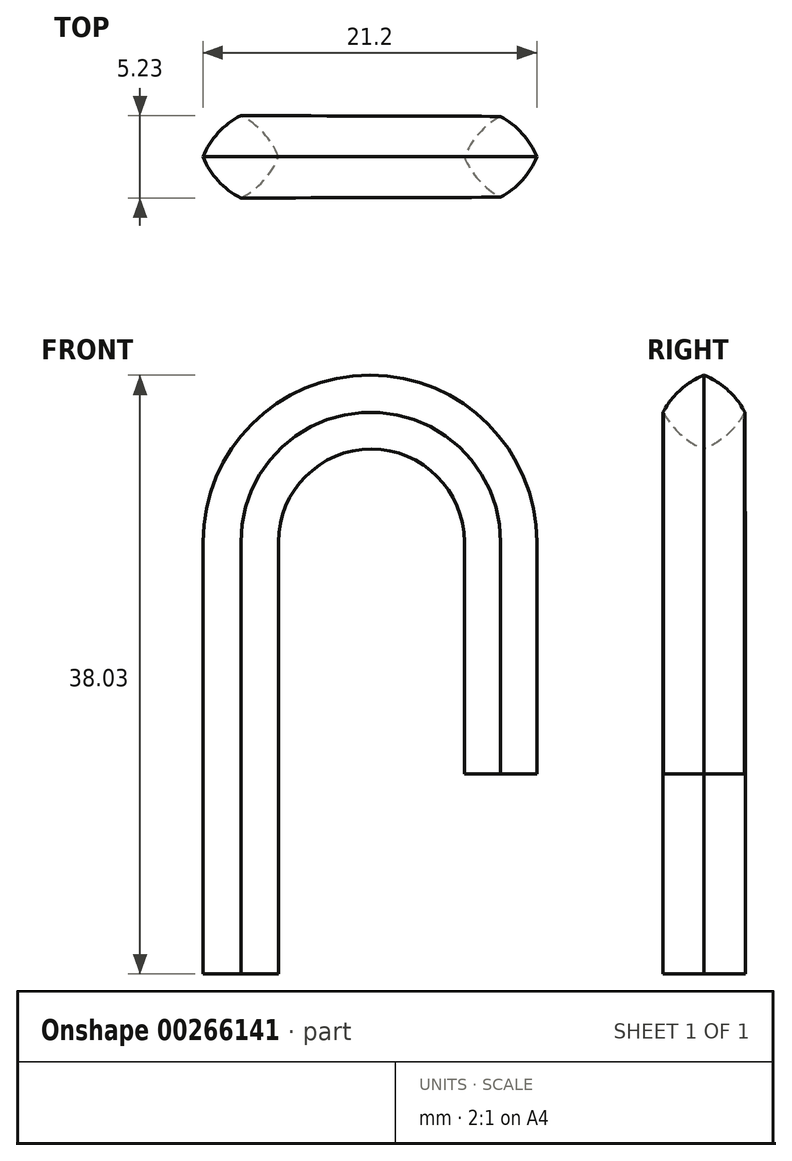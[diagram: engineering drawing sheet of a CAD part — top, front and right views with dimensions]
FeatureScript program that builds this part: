
annotation { "Feature Type Name" : "Feature", "Feature Type Description" : "" }
export const myFeature = defineFeature(function(context is Context, id is Id, definition is map)
    precondition{}
    {
        {
            var Q0;
            Q0=qCreatedBy(makeId("Front.planeOp"),FACE);
            var sketch = newSketch(context, id + "F0", { "sketchPlane" : qUnion([Q0])});
            skLineSegment(sketch, "E0", {"start": v(-2.99, 0) * mm, "end": v(2.54, 0) * mm});
            skLineSegment(sketch, "E1", {"start": v(-2.99, 0) * mm, "end": v(-2.99, 14.73) * mm});
            skLineSegment(sketch, "E2", {"start": v(2.54, 0) * mm, "end": v(2.54, 14.73) * mm});
            skLineSegment(sketch, "E3", {"start": v(2.54, 14.73) * mm, "end": v(13.6, 14.73) * mm});
            skArc(sketch, "E4", {"start": v(13.6, 14.73) * mm, "mid": v(8.07, 20.26) * mm, "end": v(2.54, 14.73) * mm});
            skLineSegment(sketch, "E5", {"start": v(13.6, 14.73) * mm, "end": v(18.95, 14.73) * mm});
            skArc(sketch, "E6", {"start": v(18.95, 14.73) * mm, "mid": v(7.98, 25.7) * mm, "end": v(-2.99, 14.73) * mm});
            skLineSegment(sketch, "E7", {"start": v(13.6, 14.73) * mm, "end": v(13.6, 0) * mm});
            skLineSegment(sketch, "E8", {"start": v(18.95, 14.73) * mm, "end": v(18.95, 0) * mm});
            skLineSegment(sketch, "E9", {"start": v(13.6, 0) * mm, "end": v(18.95, 0) * mm});
            skLineSegment(sketch, "E10", {"start": v(-2.99, 0) * mm, "end": v(-2.99, -12.7) * mm});
            skLineSegment(sketch, "E11", {"start": v(2.54, 0) * mm, "end": v(2.54, -12.7) * mm});
            skLineSegment(sketch, "E12", {"start": v(2.54, -12.7) * mm, "end": v(-2.99, -12.7) * mm});
            skSolve(sketch);
        }
        {
            var Q0;
            Q0=makeQuery(id+"F0.imprint","IMPRINT",FACE,{"disambiguationData":[TD([[makeQuery(id+"F0.imprint","IMPRINT",EDGE,{"derivedFrom":sQuery(id+"F0.wireOp",EDGE,"E0")}),1.0]])]});
            var Q1;
            Q1=makeQuery(id+"F0.imprint","IMPRINT",FACE,{"disambiguationData":[TD([[makeQuery(id+"F0.imprint","IMPRINT",EDGE,{"derivedFrom":sQuery(id+"F0.wireOp",EDGE,"E5")}),-1.0]])]});
            var Q2;
            Q2=makeQuery(id+"F0.imprint","IMPRINT",FACE,{"disambiguationData":[TD([[makeQuery(id+"F0.imprint","IMPRINT",EDGE,{"derivedFrom":sQuery(id+"F0.wireOp",EDGE,"E0")}),-1.0]])]});
            extrude(context, id + "F1", {"entities" : qUnion([Q0, Q1, Q2]), "depth" : 6.35 * mm});
        }
        {
            var Q0;
            Q0=makeQuery(id+"F1.opExtrude","CAP_EDGE",EDGE,{"disambiguationData":[OSD([sQuery(id+"F0.wireOp",EDGE,"E6")])],"isStart":false});
            var Q1;
            Q1=makeQuery(id+"F1.opExtrude","CAP_EDGE",EDGE,{"disambiguationData":[OSD([sQuery(id+"F0.wireOp",EDGE,"E8")])],"isStart":true});
            var Q2;
            Q2=makeQuery(id+"F1.opExtrude","CAP_EDGE",EDGE,{"disambiguationData":[OSD([sQuery(id+"F0.wireOp",EDGE,"E2")])],"isStart":false});
            var Q3;
            Q3=makeQuery(id+"F1.opExtrude","CAP_EDGE",EDGE,{"disambiguationData":[OSD([sQuery(id+"F0.wireOp",EDGE,"E2")])],"isStart":true});
            fillet(context, id + "F2", {"entities" : qUnion([Q0, Q1, Q2, Q3]), "radius" : 5.08 * mm, "tangentPropagation" : true, "allowEdgeOverflow" : false});
        }
    });
